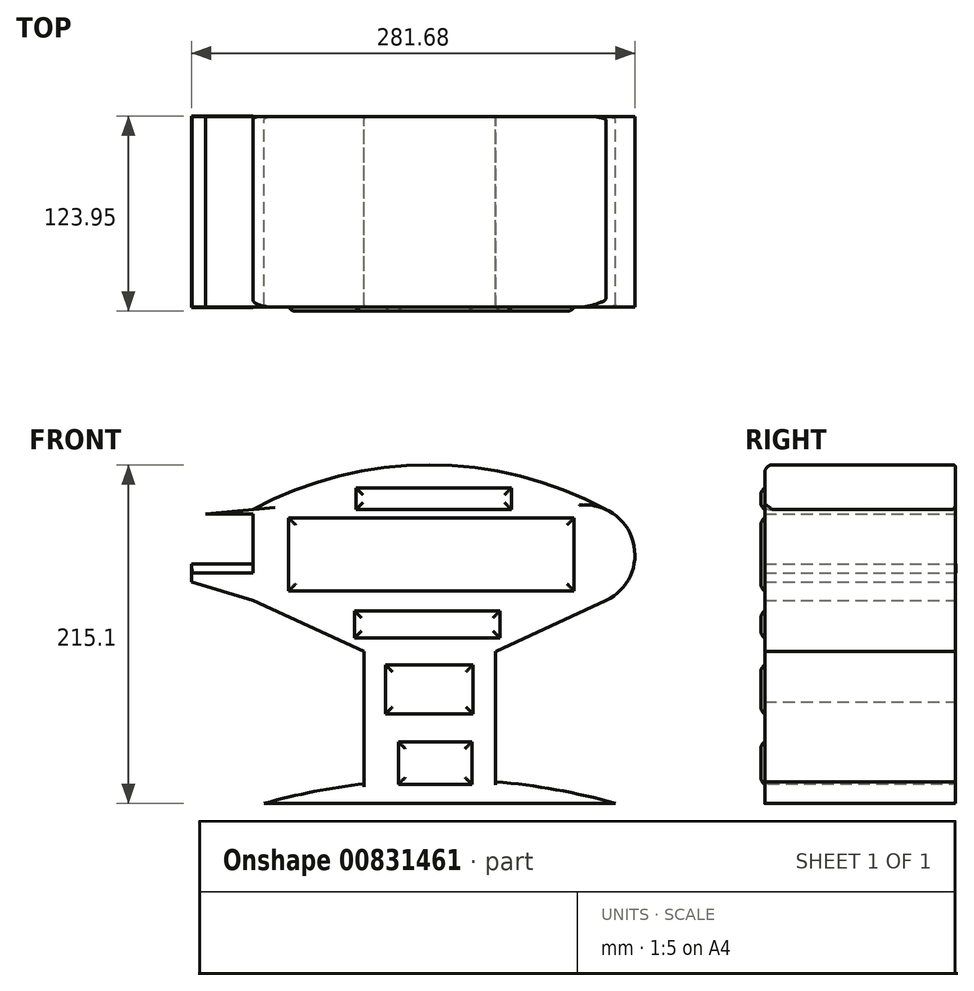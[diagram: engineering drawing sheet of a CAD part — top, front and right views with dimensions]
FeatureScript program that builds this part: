
annotation { "Feature Type Name" : "Feature", "Feature Type Description" : "" }
export const myFeature = defineFeature(function(context is Context, id is Id, definition is map)
    precondition{}
    {
        {
            var Q0;
            Q0=qCreatedBy(makeId("Front.planeOp"),FACE);
            var sketch = newSketch(context, id + "F0", { "sketchPlane" : qUnion([Q0])});
            skLineSegment(sketch, "E0.bottom", {"start": v(-45.26, -46) * mm, "end": v(38.25, -46) * mm});
            skLineSegment(sketch, "E0.top", {"start": v(-45.26, -13.73) * mm, "end": v(38.25, -13.73) * mm});
            skLineSegment(sketch, "E0.left", {"start": v(-45.26, -46) * mm, "end": v(-45.26, -13.73) * mm});
            skLineSegment(sketch, "E0.right", {"start": v(38.25, -46) * mm, "end": v(38.25, -13.73) * mm});
            skLineSegment(sketch, "E1.bottom", {"start": v(38.25, -13.73) * mm, "end": v(-45.44, -13.73) * mm});
            skLineSegment(sketch, "E1.top", {"start": v(38.25, 18.53) * mm, "end": v(-45.44, 18.53) * mm});
            skLineSegment(sketch, "E1.left", {"start": v(38.25, -13.73) * mm, "end": v(38.25, 18.53) * mm});
            skLineSegment(sketch, "E1.right", {"start": v(-45.44, -13.73) * mm, "end": v(-45.44, 18.53) * mm});
            skLineSegment(sketch, "E2.bottom", {"start": v(-45.44, 18.53) * mm, "end": v(38.36, 18.53) * mm});
            skLineSegment(sketch, "E2.top", {"start": v(-45.44, 50.87) * mm, "end": v(38.36, 50.87) * mm});
            skLineSegment(sketch, "E2.left", {"start": v(-45.44, 18.53) * mm, "end": v(-45.44, 50.87) * mm});
            skLineSegment(sketch, "E2.right", {"start": v(38.36, 18.53) * mm, "end": v(38.36, 50.87) * mm});
            skLineSegment(sketch, "E3.bottom", {"start": v(-45.44, 50.87) * mm, "end": v(-115.93, 50.87) * mm});
            skLineSegment(sketch, "E3.top", {"start": v(-45.44, 108.53) * mm, "end": v(-115.93, 108.53) * mm});
            skLineSegment(sketch, "E3.right", {"start": v(-115.93, 50.87) * mm, "end": v(-115.93, 108.53) * mm});
            skLineSegment(sketch, "E4", {"start": v(-45.44, 108.53) * mm, "end": v(38.36, 108.53) * mm});
            skLineSegment(sketch, "E5", {"start": v(38.36, 108.53) * mm, "end": v(108.3, 108.53) * mm});
            skLineSegment(sketch, "E6", {"start": v(38.36, 50.87) * mm, "end": v(108.3, 50.87) * mm});
            skLineSegment(sketch, "E7", {"start": v(-115.93, 50.87) * mm, "end": v(-45.44, 18.53) * mm});
            skLineSegment(sketch, "E8", {"start": v(38.36, 18.53) * mm, "end": v(108.3, 50.87) * mm});
            skLineSegment(sketch, "E9", {"start": v(-115.93, 108.53) * mm, "end": v(-145.89, 105.57) * mm});
            skLineSegment(sketch, "E10", {"start": v(-145.89, 105.57) * mm, "end": v(-115.93, 105.57) * mm});
            skLineSegment(sketch, "E11", {"start": v(-115.93, 50.87) * mm, "end": v(-154.96, 62.44) * mm});
            skLineSegment(sketch, "E12", {"start": v(-154.96, 62.44) * mm, "end": v(-115.93, 62.44) * mm});
            skLineSegment(sketch, "E13", {"start": v(-154.96, 62.44) * mm, "end": v(-154.96, 74) * mm});
            skLineSegment(sketch, "E14", {"start": v(-154.96, 74) * mm, "end": v(-154.96, 62.44) * mm});
            skLineSegment(sketch, "E15", {"start": v(-154.96, 74) * mm, "end": v(-153.99, 62.44) * mm});
            skLineSegment(sketch, "E16", {"start": v(-154.96, 62.44) * mm, "end": v(-115.93, 68.33) * mm});
            skLineSegment(sketch, "E17", {"start": v(-154.47, 68.22) * mm, "end": v(-115.93, 68.33) * mm});
            skArc(sketch, "E18", {"start": v(108.3, 108.53) * mm, "mid": v(-3.82, 136.98) * mm, "end": v(-115.93, 108.53) * mm});
            skArc(sketch, "E19", {"start": v(108.3, 50.87) * mm, "mid": v(126.72, 79.7) * mm, "end": v(108.3, 108.53) * mm});
            skLineSegment(sketch, "E20.left", {"start": v(-45.26, -46) * mm, "end": v(-45.26, -74.78) * mm});
            skLineSegment(sketch, "E20.right", {"start": v(38.25, -46) * mm, "end": v(38.25, -74.78) * mm});
            skLineSegment(sketch, "E21.top", {"start": v(-45.26, -78.12) * mm, "end": v(38.25, -78.12) * mm});
            skLineSegment(sketch, "E21.left", {"start": v(-45.26, -46) * mm, "end": v(-45.26, -78.12) * mm});
            skLineSegment(sketch, "E21.right", {"start": v(38.25, -46) * mm, "end": v(38.25, -78.12) * mm});
            skArc(sketch, "E22", {"start": v(114.46, -78.12) * mm, "mid": v(2.88, -62.83) * mm, "end": v(-108.7, -78.12) * mm});
            skLineSegment(sketch, "E23", {"start": v(-108.7, -78.12) * mm, "end": v(114.46, -78.12) * mm});
            skSolve(sketch);
        }
        {
            var Q0;
            Q0 = qSketchRegion(id + "F0", true);
            extrude(context, id + "F1", {"entities" : qUnion([Q0]), "depth" : 121.16 * mm, "offsetDistance" : 25.4 * mm});
        }
        {
            var Q0;
            Q0=makeQuery(id+"F1.opExtrude","CAP_FACE",FACE,{"disambiguationData":[OSD([sQuery(id+"F0.wireOp",EDGE,"E0.left"),sQuery(id+"F0.wireOp",EDGE,"E0.right"),sQuery(id+"F0.wireOp",EDGE,"E1.bottom"),sQuery(id+"F0.wireOp",EDGE,"E1.left"),sQuery(id+"F0.wireOp",EDGE,"E1.right"),sQuery(id+"F0.wireOp",EDGE,"E2.bottom"),sQuery(id+"F0.wireOp",EDGE,"E3.right"),sQuery(id+"F0.wireOp",EDGE,"E7"),sQuery(id+"F0.wireOp",EDGE,"E8"),sQuery(id+"F0.wireOp",EDGE,"E9"),sQuery(id+"F0.wireOp",EDGE,"E10"),sQuery(id+"F0.wireOp",EDGE,"E11"),sQuery(id+"F0.wireOp",EDGE,"E14"),sQuery(id+"F0.wireOp",EDGE,"E15"),sQuery(id+"F0.wireOp",EDGE,"E17"),sQuery(id+"F0.wireOp",EDGE,"E18"),sQuery(id+"F0.wireOp",EDGE,"E19"),sQuery(id+"F0.wireOp",EDGE,"E21.top"),sQuery(id+"F0.wireOp",EDGE,"E21.left"),sQuery(id+"F0.wireOp",EDGE,"E21.right")])],"isStart":false});
            var sketch = newSketch(context, id + "F2", { "sketchPlane" : qUnion([Q0])});
            skLineSegment(sketch, "E24", {"start": v(-154.96, 74) * mm, "end": v(-115.93, 74) * mm});
            skLineSegment(sketch, "E25", {"start": v(-115.93, 74) * mm, "end": v(-154.47, 68.22) * mm});
            skLineSegment(sketch, "E26", {"start": v(-154.47, 68.22) * mm, "end": v(-154.96, 74) * mm});
            skLineSegment(sketch, "E27", {"start": v(-115.93, 68.33) * mm, "end": v(-115.93, 74) * mm});
            skSolve(sketch);
        }
        {
            var Q0;
            Q0 = qSketchRegion(id + "F2", true);
            extrude(context, id + "F3", {"entities" : qUnion([Q0]), "depth" : 0.25 * mm, "offsetDistance" : 25.4 * mm});
        }
        {
            var Q0;
            Q0=makeQuery(id+"F2.imprint","IMPRINT",FACE,{"disambiguationData":[TD([[makeQuery(id+"F2.imprint","IMPRINT",EDGE,{"derivedFrom":sQuery(id+"F2.wireOp",EDGE,"E25")}),1.0]])]});
            var Q1;
            Q1=makeQuery(id+"F2.imprint","IMPRINT",FACE,{"disambiguationData":[TD([[makeQuery(id+"F2.imprint","IMPRINT",EDGE,{"derivedFrom":sQuery(id+"F2.wireOp",EDGE,"E24")}),-1.0]])]});
            extrude(context, id + "F4", {"entities" : qUnion([Q0, Q1]), "operationType" : NewBodyOperationType.ADD, "depth" : 0.25 * mm, "offsetDistance" : 25.4 * mm});
        }
        {
            var Q0;
            Q0=makeQuery(id+"F1.opExtrude","CAP_FACE",FACE,{"disambiguationData":[OSD([sQuery(id+"F0.wireOp",EDGE,"E0.left"),sQuery(id+"F0.wireOp",EDGE,"E0.right"),sQuery(id+"F0.wireOp",EDGE,"E1.bottom"),sQuery(id+"F0.wireOp",EDGE,"E1.left"),sQuery(id+"F0.wireOp",EDGE,"E1.right"),sQuery(id+"F0.wireOp",EDGE,"E2.bottom"),sQuery(id+"F0.wireOp",EDGE,"E3.right"),sQuery(id+"F0.wireOp",EDGE,"E7"),sQuery(id+"F0.wireOp",EDGE,"E8"),sQuery(id+"F0.wireOp",EDGE,"E9"),sQuery(id+"F0.wireOp",EDGE,"E10"),sQuery(id+"F0.wireOp",EDGE,"E11"),sQuery(id+"F0.wireOp",EDGE,"E14"),sQuery(id+"F0.wireOp",EDGE,"E15"),sQuery(id+"F0.wireOp",EDGE,"E17"),sQuery(id+"F0.wireOp",EDGE,"E18"),sQuery(id+"F0.wireOp",EDGE,"E19"),sQuery(id+"F0.wireOp",EDGE,"E21.top"),sQuery(id+"F0.wireOp",EDGE,"E21.left"),sQuery(id+"F0.wireOp",EDGE,"E21.right")])],"isStart":true});
            var sketch = newSketch(context, id + "F5", { "sketchPlane" : qUnion([Q0])});
            skLineSegment(sketch, "E28", {"start": v(154.96, 74) * mm, "end": v(115.93, 74) * mm});
            skLineSegment(sketch, "E29", {"start": v(115.93, 74) * mm, "end": v(115.93, 68.33) * mm});
            skLineSegment(sketch, "E30", {"start": v(115.93, 68.33) * mm, "end": v(154.96, 74) * mm});
            skSolve(sketch);
        }
        {
            var Q0;
            Q0=makeQuery(id+"F5.imprint","IMPRINT",FACE,{"disambiguationData":[TD([[makeQuery(id+"F5.imprint","IMPRINT",EDGE,{"derivedFrom":sQuery(id+"F5.wireOp",EDGE,"E28")}),1.0]])]});
            var Q1;
            Q1=makeQuery(id+"F5.imprint","IMPRINT",FACE,{"disambiguationData":[TD([[makeQuery(id+"F5.imprint","IMPRINT",EDGE,{"derivedFrom":sQuery(id+"F5.wireOp",EDGE,"E30")}),-1.0]])]});
            extrude(context, id + "F6", {"entities" : qUnion([Q0, Q1]), "depth" : 0.25 * mm, "offsetDistance" : 25.4 * mm});
        }
        {
            var Q0;
            Q0=makeQuery(id+"F1.opExtrude","CAP_FACE",FACE,{"disambiguationData":[OSD([sQuery(id+"F0.wireOp",EDGE,"E0.left"),sQuery(id+"F0.wireOp",EDGE,"E0.right"),sQuery(id+"F0.wireOp",EDGE,"E1.bottom"),sQuery(id+"F0.wireOp",EDGE,"E1.left"),sQuery(id+"F0.wireOp",EDGE,"E1.right"),sQuery(id+"F0.wireOp",EDGE,"E2.bottom"),sQuery(id+"F0.wireOp",EDGE,"E3.right"),sQuery(id+"F0.wireOp",EDGE,"E7"),sQuery(id+"F0.wireOp",EDGE,"E8"),sQuery(id+"F0.wireOp",EDGE,"E9"),sQuery(id+"F0.wireOp",EDGE,"E10"),sQuery(id+"F0.wireOp",EDGE,"E11"),sQuery(id+"F0.wireOp",EDGE,"E14"),sQuery(id+"F0.wireOp",EDGE,"E15"),sQuery(id+"F0.wireOp",EDGE,"E17"),sQuery(id+"F0.wireOp",EDGE,"E18"),sQuery(id+"F0.wireOp",EDGE,"E19"),sQuery(id+"F0.wireOp",EDGE,"E21.left"),sQuery(id+"F0.wireOp",EDGE,"E21.right"),sQuery(id+"F0.wireOp",EDGE,"E22"),sQuery(id+"F0.wireOp",EDGE,"E23")])],"isStart":false});
            var sketch = newSketch(context, id + "F7", { "sketchPlane" : qUnion([Q0])});
            skLineSegment(sketch, "E31.bottom", {"start": v(-93.12, 103.15) * mm, "end": v(88.1, 103.15) * mm});
            skLineSegment(sketch, "E31.top", {"start": v(-93.12, 56.86) * mm, "end": v(88.1, 56.86) * mm});
            skLineSegment(sketch, "E31.left", {"start": v(-93.12, 103.15) * mm, "end": v(-93.12, 56.86) * mm});
            skLineSegment(sketch, "E31.right", {"start": v(88.1, 103.15) * mm, "end": v(88.1, 56.86) * mm});
            skLineSegment(sketch, "E32.bottom", {"start": v(-50.45, 122.28) * mm, "end": v(48.3, 122.28) * mm});
            skLineSegment(sketch, "E32.top", {"start": v(-50.45, 108.53) * mm, "end": v(48.3, 108.53) * mm});
            skLineSegment(sketch, "E32.left", {"start": v(-50.45, 122.28) * mm, "end": v(-50.45, 108.53) * mm});
            skLineSegment(sketch, "E32.right", {"start": v(48.3, 122.28) * mm, "end": v(48.3, 108.53) * mm});
            skLineSegment(sketch, "E33.bottom", {"start": v(-51.35, 44.11) * mm, "end": v(40.92, 44.11) * mm});
            skLineSegment(sketch, "E33.top", {"start": v(-51.35, 27.03) * mm, "end": v(40.92, 27.03) * mm});
            skLineSegment(sketch, "E33.left", {"start": v(-51.35, 44.11) * mm, "end": v(-51.35, 27.03) * mm});
            skLineSegment(sketch, "E33.right", {"start": v(40.92, 44.11) * mm, "end": v(40.92, 27.03) * mm});
            skLineSegment(sketch, "E34.bottom", {"start": v(-31.66, 9.88) * mm, "end": v(23.84, 9.88) * mm});
            skLineSegment(sketch, "E34.top", {"start": v(-31.66, -21.23) * mm, "end": v(23.84, -21.23) * mm});
            skLineSegment(sketch, "E34.left", {"start": v(-31.66, 9.88) * mm, "end": v(-31.66, -21.23) * mm});
            skLineSegment(sketch, "E34.right", {"start": v(23.84, 9.88) * mm, "end": v(23.84, -21.23) * mm});
            skLineSegment(sketch, "E35.bottom", {"start": v(-23.56, -38.96) * mm, "end": v(23.17, -38.96) * mm});
            skLineSegment(sketch, "E35.top", {"start": v(-23.56, -66.04) * mm, "end": v(23.17, -66.04) * mm});
            skLineSegment(sketch, "E35.left", {"start": v(-23.56, -38.96) * mm, "end": v(-23.56, -66.04) * mm});
            skLineSegment(sketch, "E35.right", {"start": v(23.17, -38.96) * mm, "end": v(23.17, -66.04) * mm});
            skSolve(sketch);
        }
        {
            var Q0;
            Q0 = qSketchRegion(id + "F7", true);
            extrude(context, id + "F8", {"entities" : qUnion([Q0]), "operationType" : NewBodyOperationType.ADD, "depth" : 2.54 * mm, "offsetDistance" : 25.4 * mm});
        }
        {
            var Q0;
            Q0=makeQuery(id+"F8.opExtrude","CAP_FACE",FACE,{"disambiguationData":[OSD([sQuery(id+"F7.wireOp",EDGE,"E31.bottom"),sQuery(id+"F7.wireOp",EDGE,"E31.top"),sQuery(id+"F7.wireOp",EDGE,"E31.left"),sQuery(id+"F7.wireOp",EDGE,"E31.right")])],"isStart":false});
            var Q1;
            Q1=makeQuery(id+"F8.opExtrude","CAP_FACE",FACE,{"disambiguationData":[OSD([sQuery(id+"F7.wireOp",EDGE,"E32.bottom"),sQuery(id+"F7.wireOp",EDGE,"E32.top"),sQuery(id+"F7.wireOp",EDGE,"E32.left"),sQuery(id+"F7.wireOp",EDGE,"E32.right")])],"isStart":false});
            var Q2;
            Q2=makeQuery(id+"F8.opExtrude","CAP_FACE",FACE,{"disambiguationData":[OSD([sQuery(id+"F7.wireOp",EDGE,"E33.bottom"),sQuery(id+"F7.wireOp",EDGE,"E33.top"),sQuery(id+"F7.wireOp",EDGE,"E33.left"),sQuery(id+"F7.wireOp",EDGE,"E33.right")])],"isStart":false});
            var Q3;
            Q3=makeQuery(id+"F8.opExtrude","CAP_FACE",FACE,{"disambiguationData":[OSD([sQuery(id+"F7.wireOp",EDGE,"E34.bottom"),sQuery(id+"F7.wireOp",EDGE,"E34.top"),sQuery(id+"F7.wireOp",EDGE,"E34.left"),sQuery(id+"F7.wireOp",EDGE,"E34.right")])],"isStart":false});
            var Q4;
            Q4=makeQuery(id+"F8.opExtrude","CAP_FACE",FACE,{"disambiguationData":[OSD([sQuery(id+"F7.wireOp",EDGE,"E35.bottom"),sQuery(id+"F7.wireOp",EDGE,"E35.top"),sQuery(id+"F7.wireOp",EDGE,"E35.left"),sQuery(id+"F7.wireOp",EDGE,"E35.right")])],"isStart":false});
            fillet(context, id + "F9", {"entities" : qUnion([Q0, Q1, Q2, Q3, Q4]), "radius" : 5.08 * mm, "tangentPropagation" : true, "allowEdgeOverflow" : false});
        }
        {
            var Q0;
            Q0=makeQuery(id+"F1.opExtrude","CAP_EDGE",EDGE,{"disambiguationData":[OSD([sQuery(id+"F0.wireOp",EDGE,"E18")])],"isStart":false});
            fillet(context, id + "F10", {"entities" : qUnion([Q0]), "radius" : 5.08 * mm, "tangentPropagation" : true, "allowEdgeOverflow" : false});
        }
        {
            var Q0;
            Q0=makeQuery(id+"F1.opExtrude","CAP_EDGE",EDGE,{"disambiguationData":[OSD([sQuery(id+"F0.wireOp",EDGE,"E18")])],"isStart":true});
            var Q1;
            {var subQ0=sQuery(id+"F0.wireOp",EDGE,"E22");Q1=makeQuery(id+"F1.opExtrude","CAP_EDGE",EDGE,{"disambiguationData":[OSD([subQ0]),TDD([makeQuery(id+"F0.imprint","IMPRINT",EDGE,{"disambiguationData":[TD([[makeQuery(id+"F0.imprint","INTERSECT",VERTEX,{"disambiguationData":[OD(0.0)],"derivedFrom":[subQ0,sQuery(id+"F0.wireOp",EDGE,"E23")]}),-1.0]])],"derivedFrom":subQ0})])],"isStart":false});}
            var Q2;
            {var subQ0=sQuery(id+"F0.wireOp",EDGE,"E22");Q2=makeQuery(id+"F1.opExtrude","CAP_EDGE",EDGE,{"disambiguationData":[OSD([subQ0]),TDD([makeQuery(id+"F0.imprint","IMPRINT",EDGE,{"disambiguationData":[TD([[makeQuery(id+"F0.imprint","INTERSECT",VERTEX,{"disambiguationData":[OD(1.0)],"derivedFrom":[subQ0,sQuery(id+"F0.wireOp",EDGE,"E23")]}),1.0]])],"derivedFrom":subQ0})])],"isStart":false});}
            var Q3;
            {var subQ0=sQuery(id+"F0.wireOp",EDGE,"E22");Q3=makeQuery(id+"F1.opExtrude","CAP_EDGE",EDGE,{"disambiguationData":[OSD([subQ0]),TDD([makeQuery(id+"F0.imprint","IMPRINT",EDGE,{"disambiguationData":[TD([[makeQuery(id+"F0.imprint","INTERSECT",VERTEX,{"disambiguationData":[OD(0.0)],"derivedFrom":[subQ0,sQuery(id+"F0.wireOp",EDGE,"E23")]}),-1.0]])],"derivedFrom":subQ0})])],"isStart":true});}
            var Q4;
            {var subQ0=sQuery(id+"F0.wireOp",EDGE,"E22");Q4=makeQuery(id+"F1.opExtrude","CAP_EDGE",EDGE,{"disambiguationData":[OSD([subQ0]),TDD([makeQuery(id+"F0.imprint","IMPRINT",EDGE,{"disambiguationData":[TD([[makeQuery(id+"F0.imprint","INTERSECT",VERTEX,{"disambiguationData":[OD(1.0)],"derivedFrom":[subQ0,sQuery(id+"F0.wireOp",EDGE,"E23")]}),1.0]])],"derivedFrom":subQ0})])],"isStart":true});}
            fillet(context, id + "F11", {"entities" : qUnion([Q0, Q1, Q2, Q3, Q4]), "radius" : 1.88 * mm, "tangentPropagation" : true, "allowEdgeOverflow" : false});
        }
    });
